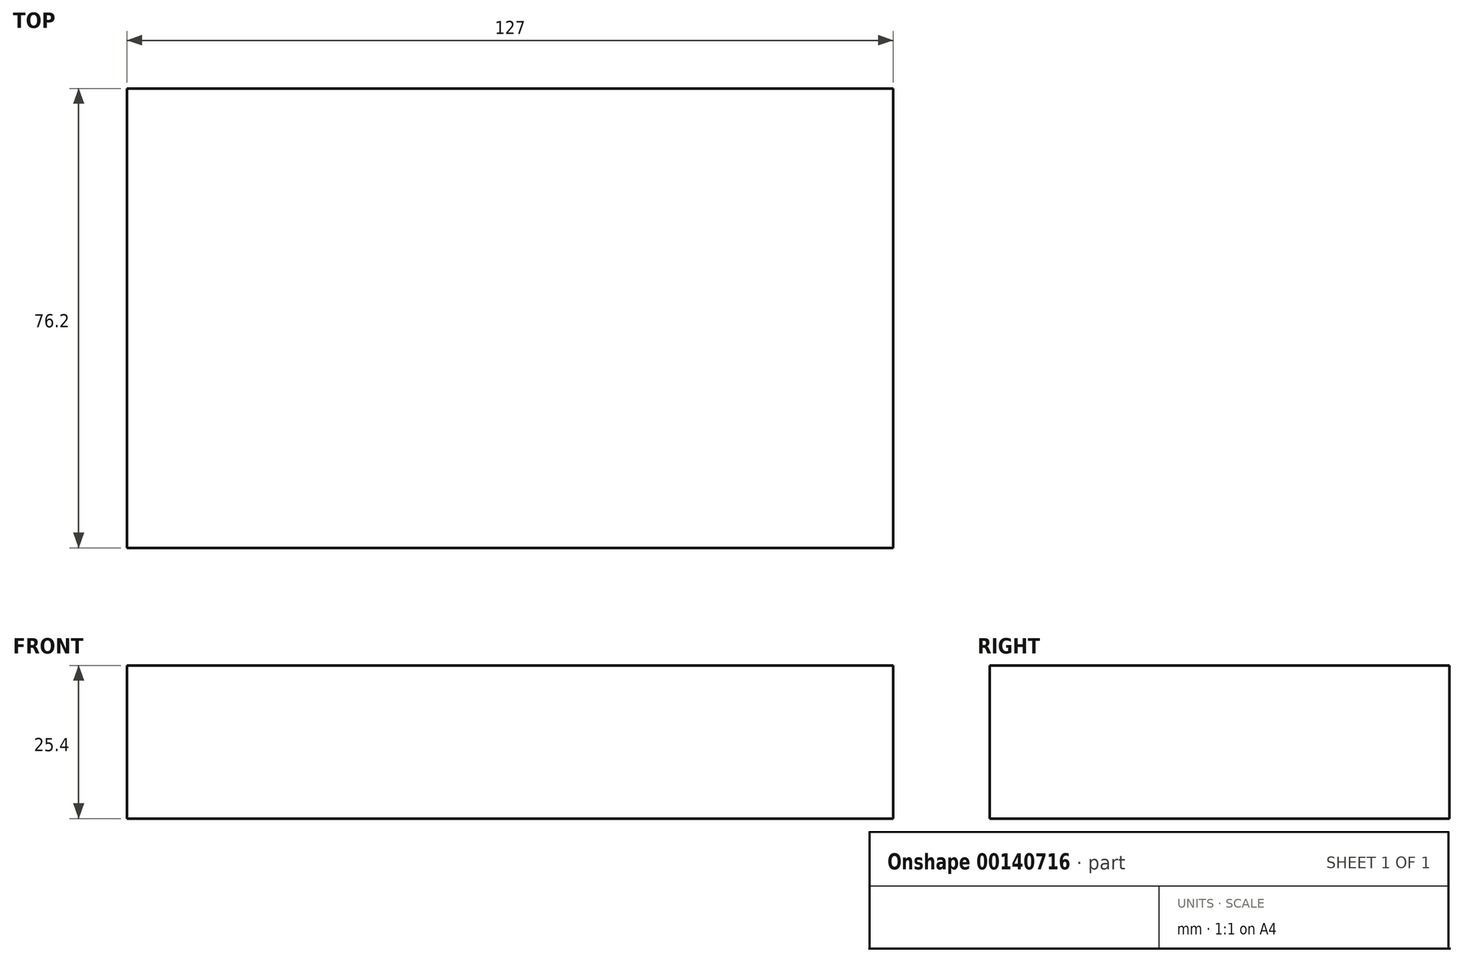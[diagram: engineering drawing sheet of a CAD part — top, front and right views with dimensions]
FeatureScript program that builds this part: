
annotation { "Feature Type Name" : "Feature", "Feature Type Description" : "" }
export const myFeature = defineFeature(function(context is Context, id is Id, definition is map)
    precondition{}
    {
        {
            var Q0;
            Q0=qCreatedBy(makeId("Top.planeOp"),FACE);
            var sketch = newSketch(context, id + "F0", { "sketchPlane" : qUnion([Q0])});
            skLineSegment(sketch, "E0.bottom", {"start": v(63.5, 38.1) * mm, "end": v(-63.5, 38.1) * mm});
            skLineSegment(sketch, "E0.top", {"start": v(63.5, -38.1) * mm, "end": v(-63.5, -38.1) * mm});
            skLineSegment(sketch, "E0.left", {"start": v(63.5, 38.1) * mm, "end": v(63.5, -38.1) * mm});
            skLineSegment(sketch, "E0.right", {"start": v(-63.5, 38.1) * mm, "end": v(-63.5, -38.1) * mm});
            skPoint(sketch, "E0.middle", {"position": v(0, 0) * mm});
            skSolve(sketch);
        }
        {
            var Q0;
            Q0 = qSketchRegion(id + "F0", true);
            extrude(context, id + "F1", {"entities" : qUnion([Q0]), "depth" : 25.4 * mm});
        }
    });
